# Revit family: Furniture-Mirrored_Cabinet-KOHLER-Verdera-K-99003
name_source: partatom
category: Specialty Equipment
revit_build: Autodesk Revit 2015 (Build: 20140606_1530(x64)
units: mm (PartAtom-declared; Revit-internal decimal feet)

## types (2) — shared parameters
ADA Compliant = No
Assembly Code = E20
Date Modified = 05/10/2018
Default Elevation = 48"
Finish = Kohler-Metal-NA-Anodized_Aluminum
Height = 30"
Length = 4 3/4"
Manufacturer = KOHLER Co.
MasterFormat 1995 = 10820
MasterFormat 2004 = 10.28.13
Material = Anodized Aluminum Construction
Product Documentation Link = http://www.us.kohler.com
Product Name = Verdera
Product Page URL = http://www.us.kohler.com
URL = https://www.us.kohler.com
Width = 20"

## per-type parameters (varying)
| type | Description | Model | Type |
| Adjustable Flip-Out Flat Mirror-NA-Anodized Aluminum Construction | aluminum medicine cabinet with adjustable flip-out flat mirror, 20IN W x 30IN H | K-99003-SCF-NA | 2 |
| Adjustable Magnifying Mirror and Slow-Close Door-NA-Anodized Aluminum Construction | 20IN W x 30IN H aluminum medicine cabinet with adjustable magnifying mirror and slow-close door | K-99003-NA | 1 |

## geometry (parser evidence)
native form markers: Sweep x10
no freeform markers — native parametric forms only
